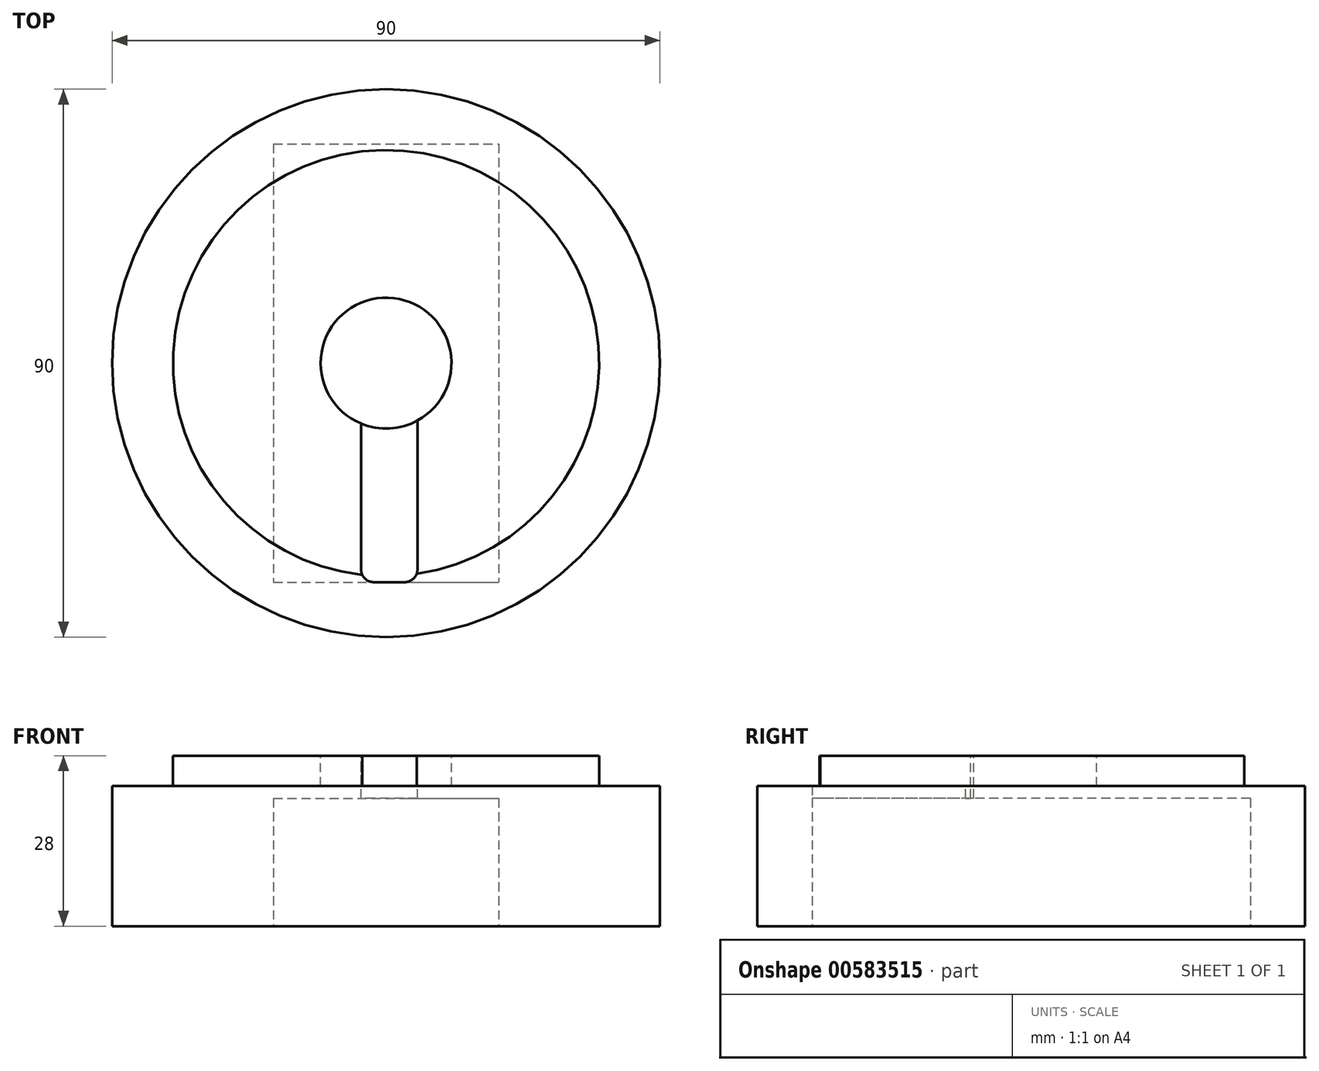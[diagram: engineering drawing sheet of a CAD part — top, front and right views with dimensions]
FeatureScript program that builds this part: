
annotation { "Feature Type Name" : "Feature", "Feature Type Description" : "" }
export const myFeature = defineFeature(function(context is Context, id is Id, definition is map)
    precondition{}
    {
        {
            var Q0;
            Q0=qCreatedBy(makeId("Top.planeOp"),FACE);
            var sketch = newSketch(context, id + "F0", { "sketchPlane" : qUnion([Q0])});
            skCircle(sketch, "E0", {"center": v(0, 0) * mm, "radius": 45 * mm});
            skSolve(sketch);
        }
        {
            var Q0;
            Q0 = qSketchRegion(id + "F0", true);
            extrude(context, id + "F1", {"entities" : qUnion([Q0]), "depth" : 28 * mm, "offsetDistance" : 25 * mm});
        }
        {
            var Q0;
            Q0=makeQuery(id+"F1.opExtrude","CAP_FACE",FACE,{"disambiguationData":[OSD([sQuery(id+"F0.wireOp",EDGE,"E0")])],"isStart":true});
            var sketch = newSketch(context, id + "F2", { "sketchPlane" : qUnion([Q0])});
            skLineSegment(sketch, "E1.bottom", {"start": v(-18.5, -36) * mm, "end": v(18.5, -36) * mm});
            skLineSegment(sketch, "E1.top", {"start": v(-18.5, 36) * mm, "end": v(18.5, 36) * mm});
            skLineSegment(sketch, "E1.left", {"start": v(-18.5, -36) * mm, "end": v(-18.5, 36) * mm});
            skLineSegment(sketch, "E1.right", {"start": v(18.5, -36) * mm, "end": v(18.5, 36) * mm});
            skPoint(sketch, "E1.middle", {"position": v(0, 0) * mm});
            skSolve(sketch);
        }
        {
            var Q0;
            Q0 = qSketchRegion(id + "F2", true);
            extrude(context, id + "F3", {"entities" : qUnion([Q0]), "operationType" : NewBodyOperationType.REMOVE, "oppositeDirection" : true, "depth" : 21 * mm, "offsetDistance" : 25 * mm});
        }
        {
            var Q0;
            Q0=makeQuery(id+"F1.opExtrude","CAP_FACE",FACE,{"disambiguationData":[OSD([sQuery(id+"F0.wireOp",EDGE,"E0")])],"isStart":false});
            var sketch = newSketch(context, id + "F4", { "sketchPlane" : qUnion([Q0])});
            skCircle(sketch, "E2", {"center": v(0, 0) * mm, "radius": 10.75 * mm});
            skSolve(sketch);
        }
        {
            var Q0;
            Q0 = qSketchRegion(id + "F4", true);
            extrude(context, id + "F5", {"entities" : qUnion([Q0]), "operationType" : NewBodyOperationType.REMOVE, "oppositeDirection" : true, "depth" : 5 * mm, "offsetDistance" : 25 * mm});
        }
        {
            var Q0;
            Q0=makeQuery(id+"F3.boolean.opBoolean","COPY",FACE,{"derivedFrom":makeQuery(id+"F3.opExtrude","CAP_FACE",FACE,{"disambiguationData":[OSD([sQuery(id+"F2.wireOp",EDGE,"E1.bottom"),sQuery(id+"F2.wireOp",EDGE,"E1.top"),sQuery(id+"F2.wireOp",EDGE,"E1.left"),sQuery(id+"F2.wireOp",EDGE,"E1.right")])],"isStart":false})});
            var sketch = newSketch(context, id + "F6", { "sketchPlane" : qUnion([Q0])});
            skArc(sketch, "E3", {"start": v(-1.99, 36) * mm, "mid": v(-4.1, 33.89) * mm, "end": v(-1.99, 31.78) * mm});
            skArc(sketch, "E4", {"start": v(3.05, 31.78) * mm, "mid": v(5.16, 33.89) * mm, "end": v(3.05, 36) * mm});
            skLineSegment(sketch, "E5", {"start": v(3.05, 31.78) * mm, "end": v(-1.99, 31.78) * mm});
            skPoint(sketch, "E6.0", {"position": v(0, 36) * mm});
            skLineSegment(sketch, "E7.0", {"start": v(-18.5, 36) * mm, "end": v(18.5, 36) * mm});
            skSolve(sketch);
        }
        {
            var Q0;
            Q0 = qSketchRegion(id + "F6", true);
            extrude(context, id + "F7", {"entities" : qUnion([Q0]), "operationType" : NewBodyOperationType.REMOVE, "oppositeDirection" : true, "depth" : 25 * mm, "offsetDistance" : 25 * mm});
        }
        {
            var Q0;
            Q0=makeQuery(id+"F1.opExtrude","CAP_FACE",FACE,{"disambiguationData":[OSD([sQuery(id+"F0.wireOp",EDGE,"E0")])],"isStart":false});
            var sketch = newSketch(context, id + "F8", { "sketchPlane" : qUnion([Q0])});
            skLineSegment(sketch, "E8", {"start": v(-4.1, -33.89) * mm, "end": v(-4.1, -9.94) * mm});
            skLineSegment(sketch, "E9", {"start": v(5.16, -33.89) * mm, "end": v(5.16, -9.43) * mm});
            skSolve(sketch);
        }
        {
            var Q0;
            Q0 = qSketchRegion(id + "F8", true);
            var Q1;
            {var subQ3=sQuery(id+"F8.wireOp",EDGE,"E8");Q1=makeQuery(id+"F8.imprint","IMPRINT",FACE,{"disambiguationData":[TD([[makeQuery(id+"F8.imprint","IMPRINT",EDGE,{"derivedFrom":subQ3}),-1.0]])]});}
            extrude(context, id + "F9", {"entities" : qUnion([Q0, Q1]), "operationType" : NewBodyOperationType.REMOVE, "oppositeDirection" : true, "depth" : 15 * mm, "offsetDistance" : 25 * mm});
        }
        {
            var Q0;
            Q0=makeQuery(id+"F1.opExtrude","CAP_FACE",FACE,{"disambiguationData":[OSD([sQuery(id+"F0.wireOp",EDGE,"E0")])],"isStart":false});
            var sketch = newSketch(context, id + "F10", { "sketchPlane" : qUnion([Q0])});
            skCircle(sketch, "E10", {"center": v(0, 0) * mm, "radius": 35 * mm});
            skCircle(sketch, "E11.0", {"center": v(0, 0) * mm, "radius": 45 * mm});
            skSolve(sketch);
        }
        {
            var Q0;
            Q0 = qSketchRegion(id + "F10", true);
            extrude(context, id + "F11", {"entities" : qUnion([Q0]), "operationType" : NewBodyOperationType.REMOVE, "oppositeDirection" : true, "depth" : 5 * mm, "offsetDistance" : 25 * mm});
        }
    });
